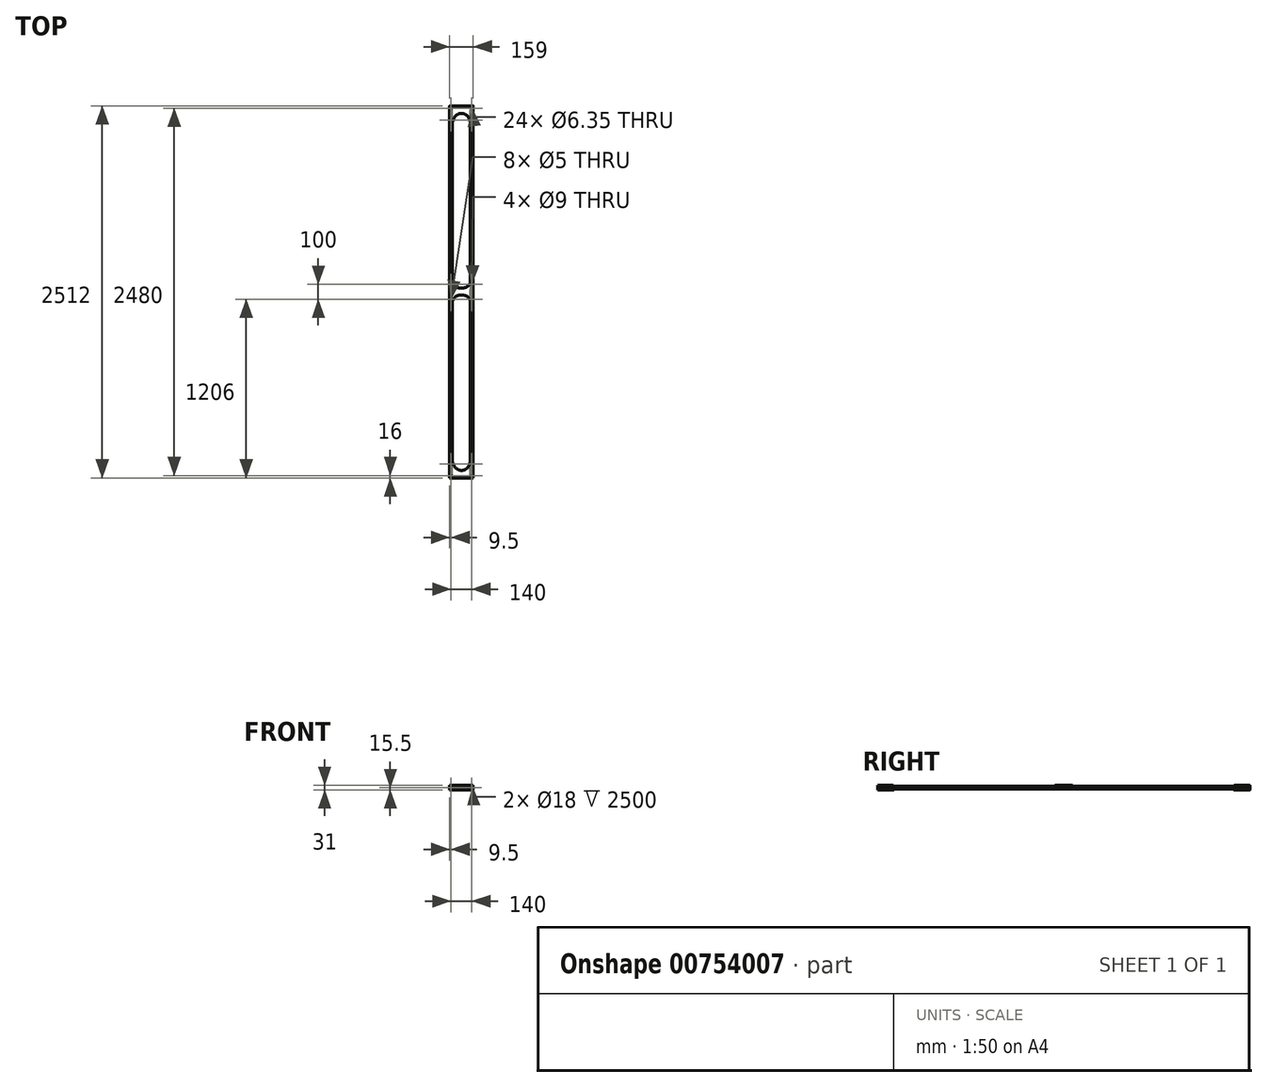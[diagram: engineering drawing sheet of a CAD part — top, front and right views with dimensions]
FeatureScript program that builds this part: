
annotation { "Feature Type Name" : "Feature", "Feature Type Description" : "" }
export const myFeature = defineFeature(function(context is Context, id is Id, definition is map)
    precondition{}
    {
        {
            var Q0;
            Q0=qCreatedBy(makeId("Front.planeOp"),FACE);
            var sketch = newSketch(context, id + "F0", { "sketchPlane" : qUnion([Q0])});
            skCircle(sketch, "E0", {"center": v(-70, 0) * mm, "radius": 9.5 * mm});
            skLineSegment(sketch, "E1", {"start": v(-70, 0) * mm, "end": v(0, 0) * mm, "construction": true});
            skCircle(sketch, "E2", {"center": v(-70, 0) * mm, "radius": 9 * mm});
            skSolve(sketch);
        }
        {
            var Q0;
            Q0=qSketchRegion(id+"F0",true);
            extrude(context, id + "F1", {"entities" : qUnion([Q0]), "endBound" : BoundingType.SYMMETRIC, "depth" : 2500 * mm, "offsetDistance" : 25 * mm});
        }
        {
            var Q0;
            Q0=makeQuery(id+"F1.opExtrude","SWEPT_BODY",BODY,{"disambiguationData":[OSD([sQuery(id+"F0.wireOp",EDGE,"E0"),sQuery(id+"F0.wireOp",EDGE,"E2")])]});
            var Q1;
            Q1=qCreatedBy(makeId("Right.planeOp"),FACE);
            mirror(context, id + "F2", {"entities" : qUnion([Q0]), "mirrorPlane" : qUnion([Q1])});
        }
        {
            var Q0;
            Q0=qCreatedBy(makeId("Top.planeOp"),FACE);
            cPlane(context, id + "F3", {"entities" : qUnion([Q0]), "cplaneType" : CPlaneType.OFFSET, "offset" : 9.5 * mm, "width" : 150 * mm, "height" : 150 * mm});
        }
        {
            var Q0;
            Q0=qCreatedBy(id+"F3.planeOp",FACE);
            var sketch = newSketch(context, id + "F4", { "sketchPlane" : qUnion([Q0])});
            skLineSegment(sketch, "E3.bottom", {"start": v(-79.5, 60) * mm, "end": v(-55, 60) * mm});
            skLineSegment(sketch, "E3.top", {"start": v(-79.5, -60) * mm, "end": v(-55, -60) * mm});
            skLineSegment(sketch, "E3.left", {"start": v(-79.5, 60) * mm, "end": v(-79.5, -60) * mm});
            skLineSegment(sketch, "E3.right", {"start": v(79.5, 60) * mm, "end": v(79.5, -60) * mm});
            skPoint(sketch, "E3.middle", {"position": v(0, 0) * mm});
            skEllipticalArc(sketch, "E4", {});
            skEllipticalArc(sketch, "E5", {});
            skLineSegment(sketch, "E6.trimOffspring", {"start": v(55, 60) * mm, "end": v(79.5, 60) * mm});
            skLineSegment(sketch, "E7.trimOffspring", {"start": v(55, -60) * mm, "end": v(79.5, -60) * mm});
            const initialGuessF4  = {"E4": [0, -0.06, -1, 0, 0.055, 0.04, 3.141592653589793, 0], "E5": [0, 0.06, -1, 0, 0.055, 0.035, 0, 3.141592653589793]};
            skSetInitialGuess(sketch, initialGuessF4);
            skSolve(sketch);
        }
        {
            var Q0;
            Q0=qSketchRegion(id+"F4",true);
            extrude(context, id + "F5", {"entities" : qUnion([Q0]), "depth" : 6 * mm, "offsetDistance" : 25 * mm});
        }
        {
            var Q0;
            Q0=makeQuery(id+"F5.opExtrude","SWEPT_EDGE",EDGE,{"disambiguationData":[OSD([sQuery(id+"F4.wireOp",EDGE,"E3.bottom"),sQuery(id+"F4.wireOp",EDGE,"E3.left")])]});
            var Q1;
            Q1=makeQuery(id+"F5.opExtrude","SWEPT_EDGE",EDGE,{"disambiguationData":[OSD([sQuery(id+"F4.wireOp",EDGE,"E3.top"),sQuery(id+"F4.wireOp",EDGE,"E3.left")])]});
            var Q2;
            Q2=makeQuery(id+"F5.opExtrude","SWEPT_EDGE",EDGE,{"disambiguationData":[OSD([sQuery(id+"F4.wireOp",EDGE,"E3.top"),sQuery(id+"F4.wireOp",EDGE,"E4")])]});
            var Q3;
            Q3=makeQuery(id+"F5.opExtrude","SWEPT_EDGE",EDGE,{"disambiguationData":[OSD([sQuery(id+"F4.wireOp",EDGE,"E4"),sQuery(id+"F4.wireOp",EDGE,"E7.trimOffspring")])]});
            var Q4;
            Q4=makeQuery(id+"F5.opExtrude","SWEPT_EDGE",EDGE,{"disambiguationData":[OSD([sQuery(id+"F4.wireOp",EDGE,"E3.right"),sQuery(id+"F4.wireOp",EDGE,"E7.trimOffspring")])]});
            var Q5;
            Q5=makeQuery(id+"F5.opExtrude","SWEPT_EDGE",EDGE,{"disambiguationData":[OSD([sQuery(id+"F4.wireOp",EDGE,"E5"),sQuery(id+"F4.wireOp",EDGE,"E6.trimOffspring")])]});
            var Q6;
            Q6=makeQuery(id+"F5.opExtrude","SWEPT_EDGE",EDGE,{"disambiguationData":[OSD([sQuery(id+"F4.wireOp",EDGE,"E3.right"),sQuery(id+"F4.wireOp",EDGE,"E6.trimOffspring")])]});
            var Q7;
            Q7=makeQuery(id+"F5.opExtrude","SWEPT_EDGE",EDGE,{"disambiguationData":[OSD([sQuery(id+"F4.wireOp",EDGE,"E3.bottom"),sQuery(id+"F4.wireOp",EDGE,"E5")])]});
            fillet(context, id + "F6", {"entities" : qUnion([Q0, Q1, Q2, Q3, Q4, Q5, Q6, Q7]), "radius" : 10 * mm, "tangentPropagation" : true, "allowEdgeOverflow" : false});
        }
        {
            var Q0;
            Q0=qCreatedBy(id+"F3.planeOp",FACE);
            var sketch = newSketch(context, id + "F7", { "sketchPlane" : qUnion([Q0])});
            skCircle(sketch, "E8", {"center": v(-70, 50) * mm, "radius": 2.5 * mm});
            skCircle(sketch, "E9", {"center": v(70, 50) * mm, "radius": 2.5 * mm});
            skCircle(sketch, "E10", {"center": v(70, -50) * mm, "radius": 2.5 * mm});
            skCircle(sketch, "E11", {"center": v(-70, -50) * mm, "radius": 2.5 * mm});
            skLineSegment(sketch, "E12", {"start": v(-70, 50) * mm, "end": v(-70, -50) * mm, "construction": true});
            skLineSegment(sketch, "E13", {"start": v(-70, -50) * mm, "end": v(70, -50) * mm, "construction": true});
            skLineSegment(sketch, "E14", {"start": v(70, 50) * mm, "end": v(70, -50) * mm, "construction": true});
            skLineSegment(sketch, "E15", {"start": v(70, 50) * mm, "end": v(-70, 50) * mm, "construction": true});
            skLineSegment(sketch, "E16", {"start": v(0, 0) * mm, "end": v(-70, 0) * mm, "construction": true});
            skLineSegment(sketch, "E17", {"start": v(0, 0) * mm, "end": v(70, 0) * mm, "construction": true});
            skLineSegment(sketch, "E18", {"start": v(0, 0) * mm, "end": v(0, 50) * mm, "construction": true});
            skLineSegment(sketch, "E19", {"start": v(0, 0) * mm, "end": v(0, -50) * mm, "construction": true});
            skSolve(sketch);
        }
        {
            var Q0;
            Q0=qSketchRegion(id+"F7",true);
            extrude(context, id + "F8", {"entities" : qUnion([Q0]), "operationType" : NewBodyOperationType.REMOVE, "endBound" : BoundingType.THROUGH_ALL, "depth" : 25 * mm, "offsetDistance" : 25 * mm, "hasSecondDirection" : true, "secondDirectionOppositeDirection" : true, "secondDirectionDepth" : 5 * mm});
        }
        {
            var Q0;
            Q0=qCreatedBy(id+"F3.planeOp",FACE);
            var sketch = newSketch(context, id + "F9", { "sketchPlane" : qUnion([Q0])});
            skLineSegment(sketch, "E20.bottom", {"start": v(-79.5, -1250) * mm, "end": v(79.5, -1250) * mm});
            skLineSegment(sketch, "E20.top", {"start": v(-79.5, -1150) * mm, "end": v(-55, -1150) * mm});
            skLineSegment(sketch, "E20.left", {"start": v(-79.5, -1250) * mm, "end": v(-79.5, -1150) * mm});
            skLineSegment(sketch, "E20.right", {"start": v(79.5, -1250) * mm, "end": v(79.5, -1150) * mm});
            skArc(sketch, "E21", {"start": v(-55, -1150) * mm, "mid": v(0, -1205) * mm, "end": v(55, -1150) * mm});
            skLineSegment(sketch, "E22.trimOffspring", {"start": v(55, -1150) * mm, "end": v(79.5, -1150) * mm});
            skSolve(sketch);
        }
        {
            var Q0;
            Q0=qSketchRegion(id+"F9",true);
            extrude(context, id + "F10", {"entities" : qUnion([Q0]), "depth" : 6 * mm, "offsetDistance" : 25 * mm});
        }
        {
            var Q0;
            Q0=makeQuery(id+"F10.opExtrude","SWEPT_EDGE",EDGE,{"disambiguationData":[OSD([sQuery(id+"F9.wireOp",EDGE,"E20.top"),sQuery(id+"F9.wireOp",EDGE,"E20.left")])]});
            var Q1;
            Q1=makeQuery(id+"F10.opExtrude","SWEPT_EDGE",EDGE,{"disambiguationData":[OSD([sQuery(id+"F9.wireOp",EDGE,"E20.top"),sQuery(id+"F9.wireOp",EDGE,"E21")])]});
            var Q2;
            Q2=makeQuery(id+"F10.opExtrude","SWEPT_EDGE",EDGE,{"disambiguationData":[OSD([sQuery(id+"F9.wireOp",EDGE,"E21"),sQuery(id+"F9.wireOp",EDGE,"E22.trimOffspring")])]});
            var Q3;
            Q3=makeQuery(id+"F10.opExtrude","SWEPT_EDGE",EDGE,{"disambiguationData":[OSD([sQuery(id+"F9.wireOp",EDGE,"E20.right"),sQuery(id+"F9.wireOp",EDGE,"E22.trimOffspring")])]});
            fillet(context, id + "F11", {"entities" : qUnion([Q0, Q1, Q2, Q3]), "radius" : 10 * mm, "tangentPropagation" : true, "allowEdgeOverflow" : false});
        }
        {
            var Q0;
            Q0=makeQuery(id+"F10.opExtrude","SWEPT_BODY",BODY,{"disambiguationData":[OSD([sQuery(id+"F9.wireOp",EDGE,"E20.bottom"),sQuery(id+"F9.wireOp",EDGE,"E20.top"),sQuery(id+"F9.wireOp",EDGE,"E20.left"),sQuery(id+"F9.wireOp",EDGE,"E20.right")])]});
            var Q1;
            Q1=qCreatedBy(makeId("Top.planeOp"),FACE);
            mirror(context, id + "F12", {"entities" : qUnion([Q0]), "mirrorPlane" : qUnion([Q1])});
        }
        {
            var Q0;
            Q0=makeQuery(id+"F10.opExtrude","CAP_FACE",FACE,{"disambiguationData":[OSD([sQuery(id+"F9.wireOp",EDGE,"E20.bottom"),sQuery(id+"F9.wireOp",EDGE,"E20.top"),sQuery(id+"F9.wireOp",EDGE,"E20.left"),sQuery(id+"F9.wireOp",EDGE,"E20.right")])],"isStart":false});
            var sketch = newSketch(context, id + "F13", { "sketchPlane" : qUnion([Q0])});
            skPoint(sketch, "E23.startSnap0", {"position": v(-66.86, -1150) * mm});
            skLineSegment(sketch, "E24", {"start": v(0, -1200) * mm, "end": v(-70, -1200) * mm, "construction": true});
            skLineSegment(sketch, "E25", {"start": v(0, -1200) * mm, "end": v(70, -1200) * mm, "construction": true});
            skLineSegment(sketch, "E26", {"start": v(-70, -1240) * mm, "end": v(0, -1240) * mm, "construction": true});
            skLineSegment(sketch, "E27", {"start": v(0, -1240) * mm, "end": v(70, -1240) * mm, "construction": true});
            skLineSegment(sketch, "E28", {"start": v(0, -1240) * mm, "end": v(0, -1200) * mm, "construction": true});
            skLineSegment(sketch, "E29", {"start": v(70, -1160) * mm, "end": v(70, -1200) * mm, "construction": true});
            skLineSegment(sketch, "E30", {"start": v(70, -1240) * mm, "end": v(70, -1200) * mm, "construction": true});
            skLineSegment(sketch, "E31", {"start": v(-70, -1160) * mm, "end": v(-70, -1200) * mm, "construction": true});
            skLineSegment(sketch, "E32", {"start": v(-70, -1240) * mm, "end": v(-70, -1200) * mm, "construction": true});
            skCircle(sketch, "E33", {"center": v(-70, -1160) * mm, "radius": 3.17 * mm});
            skCircle(sketch, "E34", {"center": v(70, -1160) * mm, "radius": 3.17 * mm});
            skCircle(sketch, "E35", {"center": v(70, -1240) * mm, "radius": 3.17 * mm});
            skCircle(sketch, "E36", {"center": v(-70, -1240) * mm, "radius": 3.17 * mm});
            skLineSegment(sketch, "E37", {"start": v(-70, -1160) * mm, "end": v(0, -1160) * mm, "construction": true});
            skLineSegment(sketch, "E38", {"start": v(0, -1160) * mm, "end": v(70, -1160) * mm, "construction": true});
            skLineSegment(sketch, "E39", {"start": v(0, -1160) * mm, "end": v(0, -1200) * mm, "construction": true});
            skSolve(sketch);
        }
        {
            var Q0;
            Q0=qSketchRegion(id+"F13",true);
            extrude(context, id + "F14", {"entities" : qUnion([Q0]), "operationType" : NewBodyOperationType.REMOVE, "endBound" : BoundingType.THROUGH_ALL, "oppositeDirection" : true, "depth" : 25 * mm, "offsetDistance" : 25 * mm});
        }
        {
            var Q0;
            Q0=makeQuery(id+"F10.opExtrude","SWEPT_BODY",BODY,{"disambiguationData":[OSD([sQuery(id+"F9.wireOp",EDGE,"E20.bottom"),sQuery(id+"F9.wireOp",EDGE,"E20.top"),sQuery(id+"F9.wireOp",EDGE,"E20.left"),sQuery(id+"F9.wireOp",EDGE,"E20.right")])]});
            var Q1;
            Q1=makeQuery(id+"F12.opPattern","COPY",BODY,{"derivedFrom":makeQuery(id+"F10.opExtrude","SWEPT_BODY",BODY,{"disambiguationData":[OSD([sQuery(id+"F9.wireOp",EDGE,"E20.bottom"),sQuery(id+"F9.wireOp",EDGE,"E20.top"),sQuery(id+"F9.wireOp",EDGE,"E20.left"),sQuery(id+"F9.wireOp",EDGE,"E20.right")])]}),"instanceName":"1"});
            var Q2;
            Q2=qCreatedBy(makeId("Front.planeOp"),FACE);
            mirror(context, id + "F15", {"entities" : qUnion([Q0, Q1]), "mirrorPlane" : qUnion([Q2])});
        }
        {
            var Q0;
            Q0=makeQuery(id+"F10.opExtrude","SWEPT_FACE",FACE,{"disambiguationData":[OSD([sQuery(id+"F9.wireOp",EDGE,"E20.bottom")])]});
            var sketch = newSketch(context, id + "F16", { "sketchPlane" : qUnion([Q0])});
            skPoint(sketch, "E40", {"position": v(79.5, -15.5) * mm});
            skLineSegment(sketch, "E41.bottom", {"start": v(-79.5, 15.5) * mm, "end": v(79.5, 15.5) * mm});
            skLineSegment(sketch, "E41.top", {"start": v(-79.5, -15.5) * mm, "end": v(79.5, -15.5) * mm});
            skLineSegment(sketch, "E41.left", {"start": v(-79.5, 15.5) * mm, "end": v(-79.5, -15.5) * mm});
            skLineSegment(sketch, "E41.right", {"start": v(79.5, 15.5) * mm, "end": v(79.5, -15.5) * mm});
            skSolve(sketch);
        }
        {
            var Q0;
            Q0=qSketchRegion(id+"F16",true);
            extrude(context, id + "F17", {"entities" : qUnion([Q0]), "depth" : 6 * mm, "offsetDistance" : 25 * mm});
        }
        {
            var Q0;
            Q0=makeQuery(id+"F17.opExtrude","SWEPT_BODY",BODY,{"disambiguationData":[OSD([sQuery(id+"F16.wireOp",EDGE,"E41.bottom"),sQuery(id+"F16.wireOp",EDGE,"E41.top"),sQuery(id+"F16.wireOp",EDGE,"E41.left"),sQuery(id+"F16.wireOp",EDGE,"E41.right")])]});
            var Q1;
            Q1=qCreatedBy(makeId("Front.planeOp"),FACE);
            mirror(context, id + "F18", {"entities" : qUnion([Q0]), "mirrorPlane" : qUnion([Q1])});
        }
        {
            var Q0;
            Q0=qCreatedBy(makeId("Top.planeOp"),FACE);
            var sketch = newSketch(context, id + "F19", { "sketchPlane" : qUnion([Q0])});
            skPoint(sketch, "E42.0", {"position": v(70, 50) * mm});
            skPoint(sketch, "E43.0", {"position": v(70, -50) * mm});
            skPoint(sketch, "E44.0", {"position": v(-70, -50) * mm});
            skPoint(sketch, "E45.0", {"position": v(-70, 50) * mm});
            skCircle(sketch, "E46", {"center": v(70, 50) * mm, "radius": 4.5 * mm});
            skCircle(sketch, "E47", {"center": v(70, -50) * mm, "radius": 4.5 * mm});
            skCircle(sketch, "E48", {"center": v(-70, -50) * mm, "radius": 4.5 * mm});
            skCircle(sketch, "E49", {"center": v(-70, 50) * mm, "radius": 4.5 * mm});
            skSolve(sketch);
        }
        {
            var Q0;
            Q0=qSketchRegion(id+"F19",true);
            extrude(context, id + "F20", {"entities" : qUnion([Q0]), "operationType" : NewBodyOperationType.REMOVE, "endBound" : BoundingType.THROUGH_ALL, "oppositeDirection" : true, "depth" : 25 * mm, "offsetDistance" : 25 * mm});
        }
        {
            var Q0;
            Q0=makeQuery(id+"F15.opPattern","COPY",EDGE,{"derivedFrom":makeQuery(id+"F12.opPattern","COPY",EDGE,{"derivedFrom":makeQuery(id+"F10.opExtrude","CAP_EDGE",EDGE,{"disambiguationData":[OSD([sQuery(id+"F9.wireOp",EDGE,"E20.left")])],"isStart":false}),"instanceName":"1"}),"instanceName":"1"});
            var Q1;
            Q1=makeQuery(id+"F18.opPattern","COPY",EDGE,{"derivedFrom":makeQuery(id+"F17.opExtrude","SWEPT_EDGE",EDGE,{"disambiguationData":[OSD([sQuery(id+"F16.wireOp",EDGE,"E41.top"),sQuery(id+"F16.wireOp",EDGE,"E41.left")])]}),"instanceName":"1"});
            var Q2;
            Q2=makeQuery(id+"F18.opPattern","COPY",EDGE,{"derivedFrom":makeQuery(id+"F17.opExtrude","CAP_EDGE",EDGE,{"disambiguationData":[OSD([sQuery(id+"F16.wireOp",EDGE,"E41.top")])],"isStart":false}),"instanceName":"1"});
            var Q3;
            Q3=makeQuery(id+"F18.opPattern","COPY",EDGE,{"derivedFrom":makeQuery(id+"F17.opExtrude","SWEPT_EDGE",EDGE,{"disambiguationData":[OSD([sQuery(id+"F16.wireOp",EDGE,"E41.top"),sQuery(id+"F16.wireOp",EDGE,"E41.right")])]}),"instanceName":"1"});
            var Q4;
            Q4=makeQuery(id+"F18.opPattern","COPY",EDGE,{"derivedFrom":makeQuery(id+"F17.opExtrude","CAP_EDGE",EDGE,{"disambiguationData":[OSD([sQuery(id+"F16.wireOp",EDGE,"E41.left")])],"isStart":false}),"instanceName":"1"});
            var Q5;
            Q5=makeQuery(id+"F15.opPattern","COPY",EDGE,{"derivedFrom":makeQuery(id+"F10.opExtrude","CAP_EDGE",EDGE,{"disambiguationData":[OSD([sQuery(id+"F9.wireOp",EDGE,"E20.left")])],"isStart":false}),"instanceName":"1"});
            var Q6;
            Q6=makeQuery(id+"F18.opPattern","COPY",EDGE,{"derivedFrom":makeQuery(id+"F17.opExtrude","SWEPT_EDGE",EDGE,{"disambiguationData":[OSD([sQuery(id+"F16.wireOp",EDGE,"E41.bottom"),sQuery(id+"F16.wireOp",EDGE,"E41.left")])]}),"instanceName":"1"});
            var Q7;
            Q7=makeQuery(id+"F18.opPattern","COPY",EDGE,{"derivedFrom":makeQuery(id+"F17.opExtrude","CAP_EDGE",EDGE,{"disambiguationData":[OSD([sQuery(id+"F16.wireOp",EDGE,"E41.bottom")])],"isStart":false}),"instanceName":"1"});
            var Q8;
            Q8=makeQuery(id+"F18.opPattern","COPY",EDGE,{"derivedFrom":makeQuery(id+"F17.opExtrude","CAP_EDGE",EDGE,{"disambiguationData":[OSD([sQuery(id+"F16.wireOp",EDGE,"E41.right")])],"isStart":false}),"instanceName":"1"});
            var Q9;
            Q9=makeQuery(id+"F18.opPattern","COPY",EDGE,{"derivedFrom":makeQuery(id+"F17.opExtrude","SWEPT_EDGE",EDGE,{"disambiguationData":[OSD([sQuery(id+"F16.wireOp",EDGE,"E41.bottom"),sQuery(id+"F16.wireOp",EDGE,"E41.right")])]}),"instanceName":"1"});
            fillet(context, id + "F21", {"entities" : qUnion([Q0, Q1, Q2, Q3, Q4, Q5, Q6, Q7, Q8, Q9]), "radius" : 1 * mm, "tangentPropagation" : true, "allowEdgeOverflow" : false});
        }
    });
